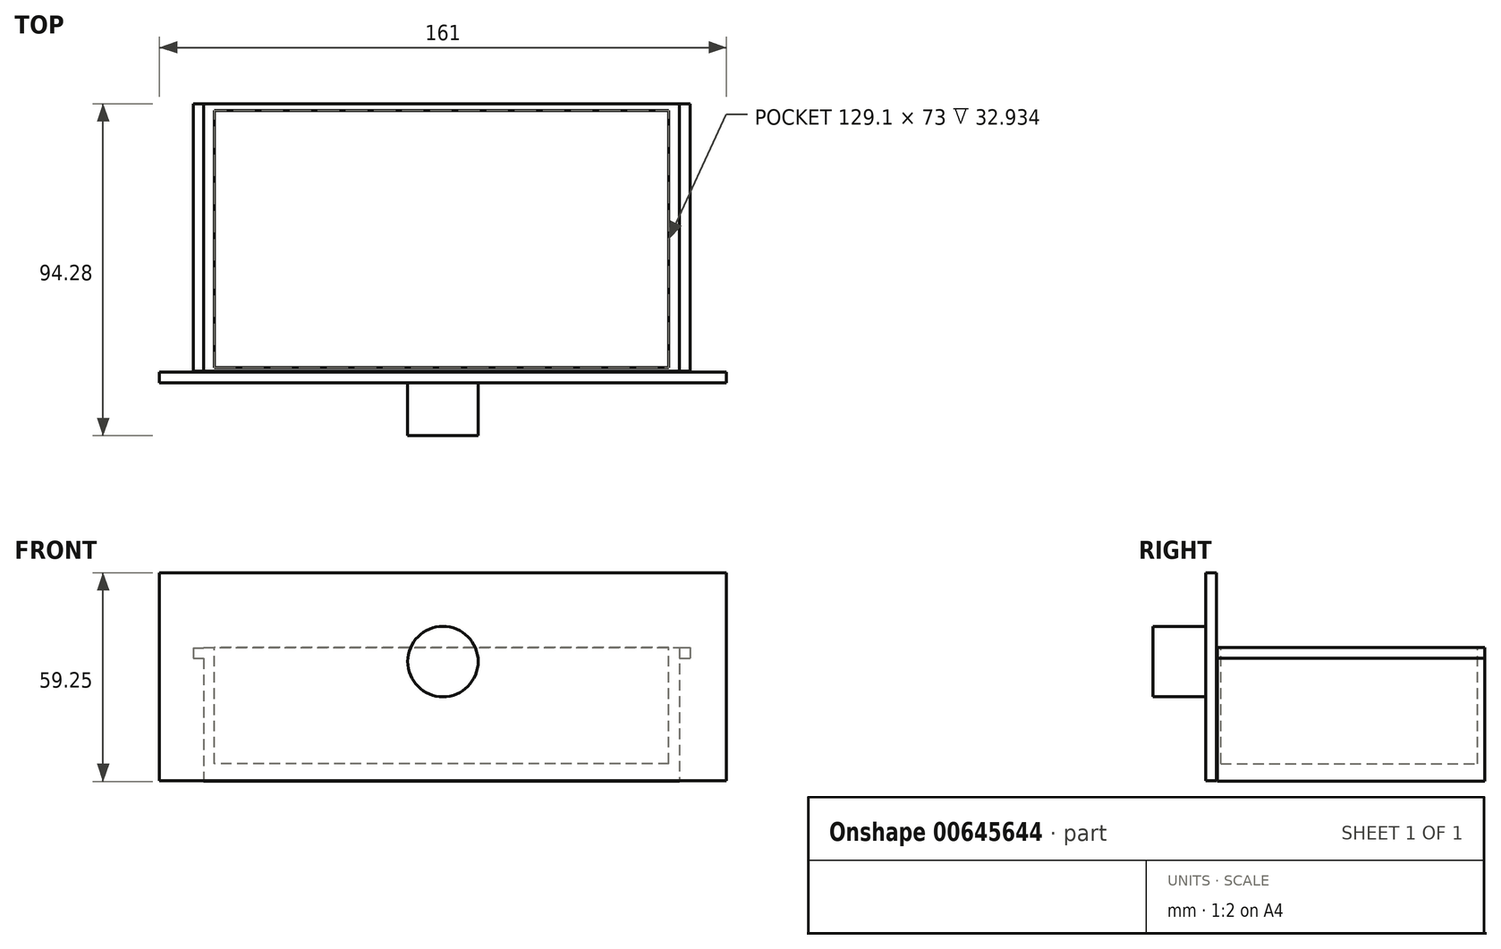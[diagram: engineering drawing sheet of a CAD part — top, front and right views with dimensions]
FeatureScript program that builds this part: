
annotation { "Feature Type Name" : "Feature", "Feature Type Description" : "" }
export const myFeature = defineFeature(function(context is Context, id is Id, definition is map)
    precondition{}
    {
        {
            var Q0;
            Q0=qCreatedBy(makeId("Front.planeOp"),FACE);
            var sketch = newSketch(context, id + "F0", { "sketchPlane" : qUnion([Q0])});
            skLineSegment(sketch, "E0.bottom", {"start": v(-67.96, -2.07) * mm, "end": v(67.14, -2.07) * mm});
            skLineSegment(sketch, "E0.top", {"start": v(-67.96, -40.07) * mm, "end": v(67.14, -40.07) * mm});
            skLineSegment(sketch, "E0.left", {"start": v(-67.96, -2.07) * mm, "end": v(-67.96, -40.07) * mm});
            skLineSegment(sketch, "E0.right", {"start": v(67.14, -2.07) * mm, "end": v(67.14, -40.07) * mm});
            skSolve(sketch);
        }
        {
            var Q0;
            Q0 = qSketchRegion(id + "F0", true);
            extrude(context, id + "F1", {"entities" : qUnion([Q0]), "depth" : 76 * mm, "offsetDistance" : 25.4 * mm});
        }
        {
            var Q0;
            Q0=qCreatedBy(makeId("Right.planeOp"),FACE);
            var sketch = newSketch(context, id + "F2", { "sketchPlane" : qUnion([Q0])});
            skLineSegment(sketch, "E1.bottom", {"start": v(-76.28, -39.82) * mm, "end": v(-79.28, -39.82) * mm});
            skLineSegment(sketch, "E1.top", {"start": v(-76.28, 19.18) * mm, "end": v(-79.28, 19.18) * mm});
            skLineSegment(sketch, "E1.left", {"start": v(-76.28, -39.82) * mm, "end": v(-76.28, 19.18) * mm});
            skLineSegment(sketch, "E1.right", {"start": v(-79.28, -39.82) * mm, "end": v(-79.28, 19.18) * mm});
            skSolve(sketch);
        }
        {
            var Q0;
            Q0 = qSketchRegion(id + "F2", true);
            extrude(context, id + "F3", {"entities" : qUnion([Q0]), "endBound" : BoundingType.SYMMETRIC, "depth" : 161 * mm, "offsetDistance" : 25.4 * mm});
        }
        {
            var Q0;
            Q0=qCreatedBy(makeId("Top.planeOp"),FACE);
            var sketch = newSketch(context, id + "F4", { "sketchPlane" : qUnion([Q0])});
            skLineSegment(sketch, "E2.bottom", {"start": v(64.14, -75) * mm, "end": v(-64.96, -75) * mm});
            skLineSegment(sketch, "E2.top", {"start": v(64.14, -2) * mm, "end": v(-64.96, -2) * mm});
            skLineSegment(sketch, "E2.left", {"start": v(64.14, -75) * mm, "end": v(64.14, -2) * mm});
            skLineSegment(sketch, "E2.right", {"start": v(-64.96, -75) * mm, "end": v(-64.96, -2) * mm});
            skSolve(sketch);
        }
        {
            var Q0;
            Q0 = qSketchRegion(id + "F4", true);
            extrude(context, id + "F5", {"entities" : qUnion([Q0]), "operationType" : NewBodyOperationType.REMOVE, "oppositeDirection" : true, "depth" : 35 * mm, "offsetDistance" : 25.4 * mm});
        }
        {
            var Q0;
            Q0=qCreatedBy(makeId("Front.planeOp"),FACE);
            var sketch = newSketch(context, id + "F6", { "sketchPlane" : qUnion([Q0])});
            skLineSegment(sketch, "E3.bottom", {"start": v(67.2, -2.03) * mm, "end": v(70.2, -2.03) * mm});
            skLineSegment(sketch, "E3.top", {"start": v(67.2, -5.03) * mm, "end": v(70.2, -5.03) * mm});
            skLineSegment(sketch, "E3.left", {"start": v(67.2, -2.03) * mm, "end": v(67.2, -5.03) * mm});
            skLineSegment(sketch, "E3.right", {"start": v(70.2, -2.03) * mm, "end": v(70.2, -5.03) * mm});
            skSolve(sketch);
        }
        {
            var Q0;
            Q0 = qSketchRegion(id + "F6", true);
            extrude(context, id + "F7", {"entities" : qUnion([Q0]), "operationType" : NewBodyOperationType.ADD, "depth" : 76 * mm, "offsetDistance" : 25.4 * mm});
        }
        {
            var Q0;
            Q0=qCreatedBy(makeId("Front.planeOp"),FACE);
            var sketch = newSketch(context, id + "F8", { "sketchPlane" : qUnion([Q0])});
            skLineSegment(sketch, "E4.bottom", {"start": v(-70.87, -2.13) * mm, "end": v(-67.87, -2.13) * mm});
            skLineSegment(sketch, "E4.top", {"start": v(-70.87, -5.13) * mm, "end": v(-67.87, -5.13) * mm});
            skLineSegment(sketch, "E4.left", {"start": v(-70.87, -2.13) * mm, "end": v(-70.87, -5.13) * mm});
            skLineSegment(sketch, "E4.right", {"start": v(-67.87, -2.13) * mm, "end": v(-67.87, -5.13) * mm});
            skSolve(sketch);
        }
        {
            var Q0;
            Q0 = qSketchRegion(id + "F8", true);
            extrude(context, id + "F9", {"entities" : qUnion([Q0]), "operationType" : NewBodyOperationType.ADD, "depth" : 76 * mm, "offsetDistance" : 25.4 * mm});
        }
        {
            var Q0;
            Q0=makeQuery(id+"F3.opExtrude","SWEPT_FACE",FACE,{"disambiguationData":[OSD([sQuery(id+"F2.wireOp",EDGE,"E1.right")])]});
            var sketch = newSketch(context, id + "F10", { "sketchPlane" : qUnion([Q0])});
            skCircle(sketch, "E5", {"center": v(0, -6.02) * mm, "radius": 10 * mm});
            skSolve(sketch);
        }
        {
            var Q0;
            Q0 = qSketchRegion(id + "F10", true);
            extrude(context, id + "F11", {"entities" : qUnion([Q0]), "operationType" : NewBodyOperationType.ADD, "depth" : 15 * mm, "offsetDistance" : 25.4 * mm});
        }
    });
